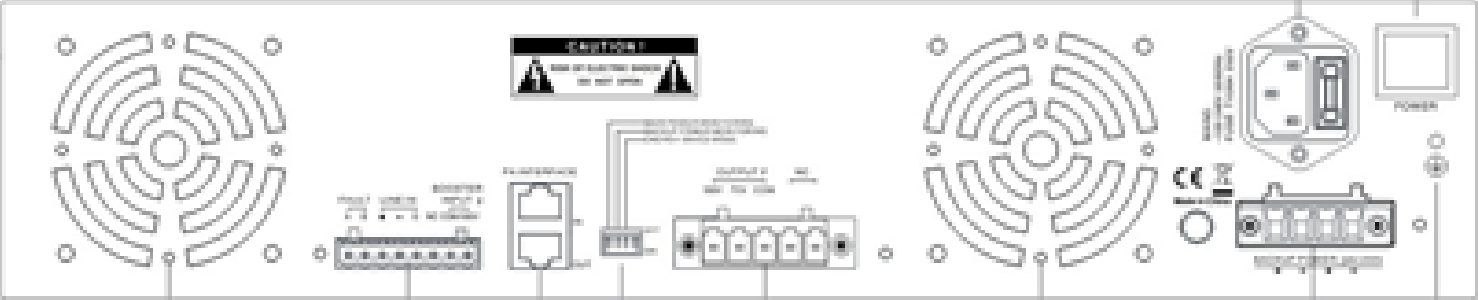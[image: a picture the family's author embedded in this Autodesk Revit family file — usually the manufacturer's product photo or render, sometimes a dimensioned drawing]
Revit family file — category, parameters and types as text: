
# Revit family: RK-MCU
name_source: partatom
category: Electrical Equipment
revit_build: Autodesk Revit 2016 (Build: 20150220_1215(x64)
units: mm (PartAtom-declared; Revit-internal decimal feet)

## family parameters
Always vertical = Yes
Cut with Voids When Loaded = No
OmniClass Number = 23.80.30.11.17
OmniClass Title = Distribution Boards and Control Panels
Panel Configuration = Two Columns, Circuits Across
Part Type = Panelboard
Room Calculation Point = No
Round Connector Dimension = Use Diameter
Shared = No
Work Plane-Based = No

## types (1)
- RK-MCU
    Access Clearance Bottom = 0 mm  [stored 0 ft]
    Access Clearance Front = 0 mm  [stored 0 ft]
    Access Clearance Left = 0 mm  [stored 0 ft]
    Access Clearance Rear = 0 mm  [stored 0 ft]
    Access Clearance Right = 0 mm  [stored 0 ft]
    Access Clearance Top = 0 mm  [stored 0 ft]
    BMS Links = Yes
    Battery Type = e.g. Alkaline, Lithium Ion Rechargeable
    CE Approval = Number, Yes, No
    Coverage Area = 0.06 m²
    Default elevation = 1219 mm
    Embodied Carbon = kgCO2
    Enclosure Rating = IP rating
    Energy Technology List = External data hyperconnection
    Environmental Product Declaration = 3rd Party Verification
    Expected Life = *Years
    Features = Free text to describe product
    Fire Control Panel Links = Yes
    Frequency = 350 Hz ~ 12 kHz
    Green Guide for Specification = A - E
    Gross Weight = 2.05Kg
    Life Cycle Analysis = A - E
    Location of Manufacturer = Northing,Easting
    Manufacturer Website = External data hyperconnection
    Material = Steel
    Material2 = cutout
    Number of Poles = 3
    O&M Manual = External data hyperconnection
    Overall Height = 165 mm
    Overall Length = 240 mm  [stored 0.787402 ft]
    Overall Width = 225 mm  [stored 0.738189 ft]
    Product Model Number = Or  Code
    Responsible Sourcing of Materials = Endorsing body
    Set Point Concentration = 0 m²
    Supply Phase = 3
    voltage = 100V/70V

note: [stored X ft] marks values corroborated as IEEE doubles in the binary element streams (Revit-internal decimal feet)

## geometry (parser evidence)
native form markers: Sweep x5
no freeform markers — native parametric forms only
